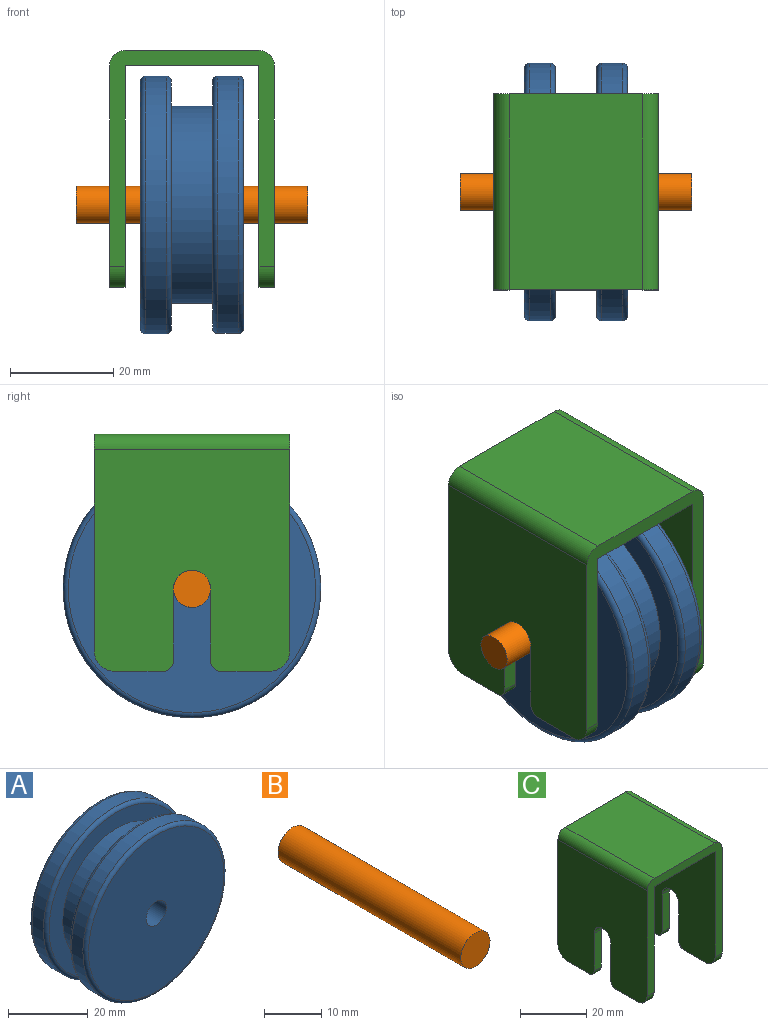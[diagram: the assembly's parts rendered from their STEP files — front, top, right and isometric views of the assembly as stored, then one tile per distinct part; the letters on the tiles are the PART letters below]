
ASSEMBLY  parts=3 mates=2
PART A: 12 faces, bbox 54.1x20x54.1 mm
  f0: cylinder r=25mm len=50mm, axis (0,-1,0), area 628.3mm2, adj f10,f11
  f1: plane 48x48mm, normal (0,1,0), area 660.5mm2, adj f3,f11
  f2: plane 48x48mm, normal (0,-1,0), area 1768.8mm2, adj f7,f10
  f3: cylinder r=19.12mm len=38.25mm, axis (0,-1,0), area 961.3mm2, adj f1,f6
  f4: cylinder r=25mm len=50mm, axis (0,-1,0), area 628.3mm2, adj f8,f9
  f5: plane 48x48mm, normal (0,1,0), area 1768.8mm2, adj f7,f9
  f6: plane 48x48mm, normal (0,-1,0), area 660.5mm2, adj f3,f8
  f7: cylinder r=3.6mm len=20mm, axis (0,1,0), area 452.4mm2, adj f2,f5
  f8: torus R=24mm, axis (0,1,0), area 243.2mm2, adj f4,f6
  f9: torus R=24mm, axis (0,1,0), area 243.2mm2, adj f4,f5
  f10: torus R=24mm, axis (0,-1,0), area 243.2mm2, adj f0,f2
  f11: torus R=24mm, axis (0,-1,0), area 243.2mm2, adj f0,f1
PART B: 3 faces, bbox 7.2x45x7.2 mm
  f0: cylinder r=3.6mm len=45mm, axis (0,-1,0), area 1017.9mm2, adj f1,f2
  f1: plane 7.2x7.2mm, normal (0,1,0), area 40.7mm2, adj f0
  f2: plane 7.2x7.2mm, normal (0,-1,0), area 40.7mm2, adj f0
PART C: 28 faces, bbox 32x38x46 mm
  f0: plane 9.4x3mm, normal (0,0,-1), area 28.2mm2, adj f2,f3,f22,f25
  f1: plane 9.4x3mm, normal (0,0,-1), area 28.2mm2, adj f4,f9,f20,f26
  f2: plane 43x38mm, normal (-1,0,0), area 1489.9mm2, adj f0,f6,f10,f11,f12,f17,f18,f19
  f3: plane 43x38mm, normal (1,0,0), area 1489.9mm2, adj f0,f6,f7,f10,f11,f17,f18,f19
  f4: plane 43x38mm, normal (-1,0,0), area 1489.9mm2, adj f1,f7,f8,f10,f11,f14,f15,f16
  f5: plane 38x26mm, normal (0,0,1), area 988mm2, adj f10,f11,f12,f13
  f6: plane 9.4x3mm, normal (0,0,-1), area 28.2mm2, adj f2,f3,f23,f27
  f7: plane 38x26mm, normal (0,0,-1), area 988mm2, adj f3,f4,f10,f11
  f8: plane 9.4x3mm, normal (0,0,-1), area 28.2mm2, adj f4,f9,f21,f24
  f9: plane 43x38mm, normal (1,0,0), area 1489.9mm2, adj f1,f8,f10,f11,f13,f14,f15,f16
  f10: plane 42x32mm, normal (0,1,0), area 326.1mm2, adj f2,f3,f4,f5,f7,f9,f12,f13
  f11: plane 42x32mm, normal (0,-1,0), area 326.1mm2, adj f2,f3,f4,f5,f7,f9,f12,f13
  f12: cylinder r=3mm len=38mm, axis (0,-1,0), area 179.1mm2, adj f2,f5,f10,f11
  f13: cylinder r=3mm len=38mm, axis (0,-1,0), area 179.1mm2, adj f5,f9,f10,f11
  f14: cylinder r=3.6mm len=7.2mm, axis (1,0,0), area 33.9mm2, adj f4,f9,f15,f16
  f15: plane 14x3mm, normal (0,1,0), area 42mm2, adj f4,f9,f14,f21
  f16: plane 14x3mm, normal (0,-1,0), area 42mm2, adj f4,f9,f14,f20
  f17: plane 14x3mm, normal (0,-1,0), area 42mm2, adj f2,f3,f19,f23
  f18: plane 14x3mm, normal (0,1,0), area 42mm2, adj f2,f3,f19,f22
  f19: cylinder r=3.6mm len=7.2mm, axis (1,0,0), area 33.9mm2, adj f2,f3,f17,f18
  f20: cylinder r=2mm len=3mm, axis (-1,0,0), area 9.4mm2, adj f1,f4,f9,f16
  f21: cylinder r=2mm len=3mm, axis (1,0,0), area 9.4mm2, adj f4,f8,f9,f15
  f22: cylinder r=2mm len=3mm, axis (-1,0,0), area 9.4mm2, adj f0,f2,f3,f18
  f23: cylinder r=2mm len=3mm, axis (1,0,0), area 9.4mm2, adj f2,f3,f6,f17
  f24: cylinder r=4mm len=4mm, axis (1,0,0), area 18.8mm2, adj f4,f8,f9,f11
  f25: cylinder r=4mm len=4mm, axis (1,0,0), area 18.8mm2, adj f0,f2,f3,f11
  f26: cylinder r=4mm len=4mm, axis (-1,0,0), area 18.8mm2, adj f1,f4,f9,f10
  f27: cylinder r=4mm len=4mm, axis (-1,0,0), area 18.8mm2, adj f2,f3,f6,f10
PLACE A rot(axis=(0,0,-1),90deg) t=(3,15,16)mm
PLACE B rot(axis=(-0.58,-0.58,-0.58),120deg) t=(-9.5,15,16)mm
PLACE C t=(-3,-4,0)mm
MATE fastened B.f0 <-> C.f14  axis (-1,0,0) through (13,15,16)mm
MATE fastened A.f3 <-> B.f0  axis (-1,0,0) through (13,15,16)mm
